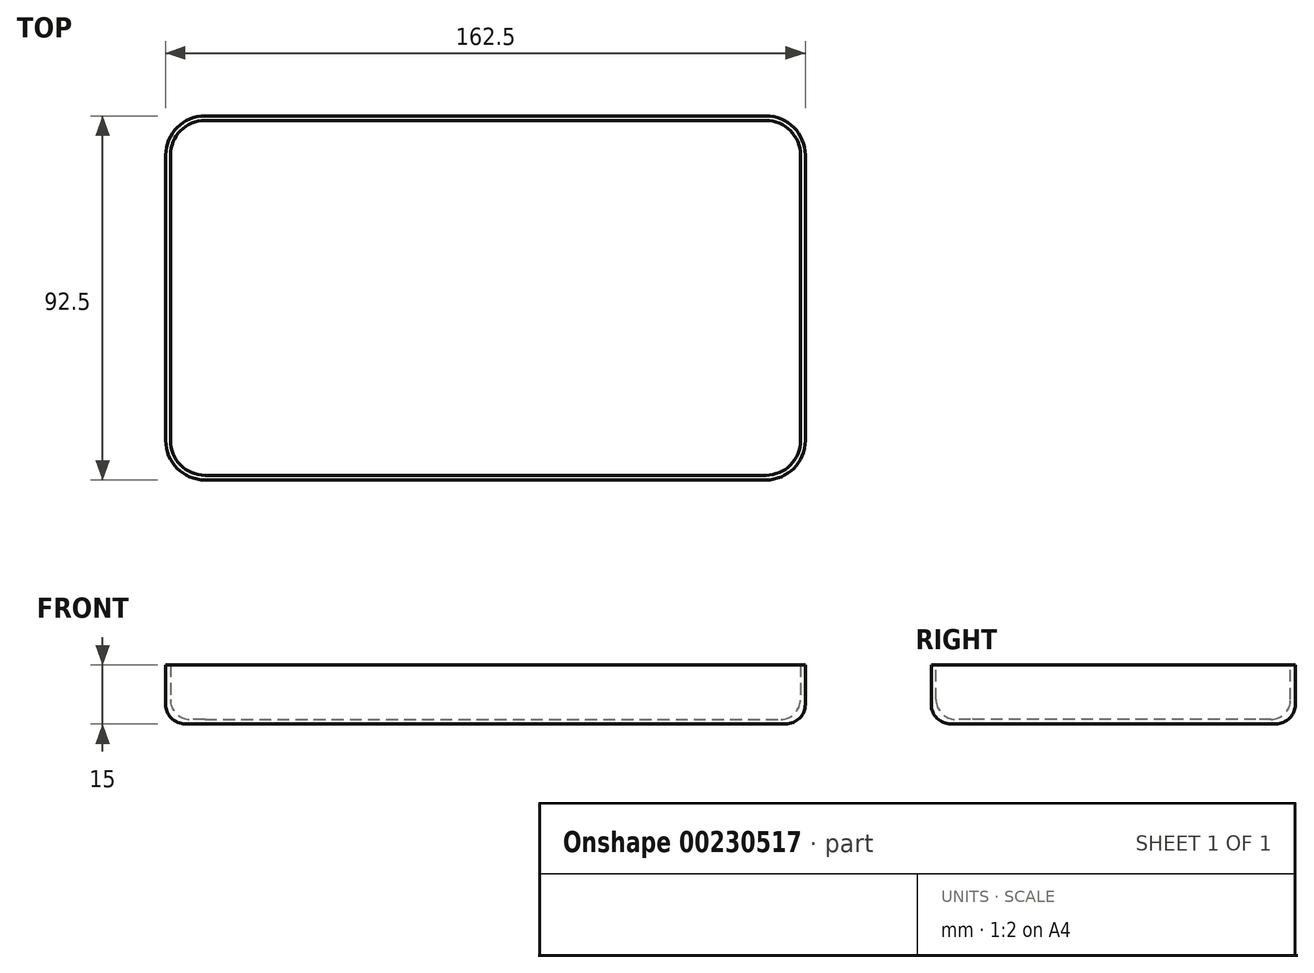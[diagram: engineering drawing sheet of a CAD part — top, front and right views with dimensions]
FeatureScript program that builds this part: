
annotation { "Feature Type Name" : "Feature", "Feature Type Description" : "" }
export const myFeature = defineFeature(function(context is Context, id is Id, definition is map)
    precondition{}
    {
        {
            var Q0;
            Q0=qCreatedBy(makeId("Top.planeOp"),FACE);
            var sketch = newSketch(context, id + "F0", { "sketchPlane" : qUnion([Q0])});
            skLineSegment(sketch, "E0.bottom", {"start": v(-107.19, 42.76) * mm, "end": v(35.31, 42.76) * mm});
            skLineSegment(sketch, "E0.top", {"start": v(-107.19, -49.74) * mm, "end": v(35.31, -49.74) * mm});
            skLineSegment(sketch, "E0.left", {"start": v(-117.19, 32.76) * mm, "end": v(-117.19, -39.74) * mm});
            skLineSegment(sketch, "E0.right", {"start": v(45.31, 32.76) * mm, "end": v(45.31, -39.74) * mm});
            skPoint(sketch, "E1.visualSharp", {"position": v(-117.19, 42.76) * mm});
            skArc(sketch, "E1.filletArc", {"start": v(-107.19, 42.76) * mm, "mid": v(-114.26, 39.84) * mm, "end": v(-117.19, 32.76) * mm});
            skPoint(sketch, "E2.visualSharp", {"position": v(-117.19, -49.74) * mm});
            skArc(sketch, "E2.filletArc", {"start": v(-117.19, -39.74) * mm, "mid": v(-114.26, -46.8) * mm, "end": v(-107.19, -49.74) * mm});
            skPoint(sketch, "E3.visualSharp", {"position": v(45.31, -49.74) * mm});
            skArc(sketch, "E3.filletArc", {"start": v(35.31, -49.74) * mm, "mid": v(42.38, -46.8) * mm, "end": v(45.31, -39.74) * mm});
            skPoint(sketch, "E4.visualSharp", {"position": v(45.31, 42.76) * mm});
            skArc(sketch, "E4.filletArc", {"start": v(45.31, 32.76) * mm, "mid": v(42.38, 39.84) * mm, "end": v(35.31, 42.76) * mm});
            skSolve(sketch);
        }
        {
            var Q0;
            Q0=qSketchRegion(id+"F0",true);
            extrude(context, id + "F1", {"entities" : qUnion([Q0]), "depth" : 15 * mm});
        }
        {
            var Q0;
            Q0=makeQuery(id+"F1.opExtrude","CAP_FACE",FACE,{"disambiguationData":[OSD([sQuery(id+"F0.wireOp",EDGE,"E0.bottom"),sQuery(id+"F0.wireOp",EDGE,"E0.top"),sQuery(id+"F0.wireOp",EDGE,"E0.left"),sQuery(id+"F0.wireOp",EDGE,"E0.right"),sQuery(id+"F0.wireOp",EDGE,"E1.filletArc"),sQuery(id+"F0.wireOp",EDGE,"E2.filletArc"),sQuery(id+"F0.wireOp",EDGE,"E3.filletArc"),sQuery(id+"F0.wireOp",EDGE,"E4.filletArc")])],"isStart":false});
            shell(context, id + "F2", {"entities" : qUnion([Q0]), "thickness" : 1.2 * mm});
        }
        {
            var Q0;
            Q0=makeQuery(id+"F2.opShell","OFFSET_FACE",FACE,{"disambiguationData":[OSD([sQuery(id+"F0.wireOp",EDGE,"E0.bottom"),sQuery(id+"F0.wireOp",EDGE,"E0.top"),sQuery(id+"F0.wireOp",EDGE,"E0.left"),sQuery(id+"F0.wireOp",EDGE,"E0.right"),sQuery(id+"F0.wireOp",EDGE,"E1.filletArc"),sQuery(id+"F0.wireOp",EDGE,"E2.filletArc"),sQuery(id+"F0.wireOp",EDGE,"E3.filletArc"),sQuery(id+"F0.wireOp",EDGE,"E4.filletArc")])]});
            fillet(context, id + "F3", {"entities" : qUnion([Q0]), "radius" : 5 * mm, "tangentPropagation" : true, "allowEdgeOverflow" : false});
        }
        {
            var Q0;
            Q0=makeQuery(id+"F1.opExtrude","CAP_FACE",FACE,{"disambiguationData":[OSD([sQuery(id+"F0.wireOp",EDGE,"E0.bottom"),sQuery(id+"F0.wireOp",EDGE,"E0.top"),sQuery(id+"F0.wireOp",EDGE,"E0.left"),sQuery(id+"F0.wireOp",EDGE,"E0.right"),sQuery(id+"F0.wireOp",EDGE,"E1.filletArc"),sQuery(id+"F0.wireOp",EDGE,"E2.filletArc"),sQuery(id+"F0.wireOp",EDGE,"E3.filletArc"),sQuery(id+"F0.wireOp",EDGE,"E4.filletArc")])],"isStart":true});
            fillet(context, id + "F4", {"entities" : qUnion([Q0]), "radius" : 5 * mm, "tangentPropagation" : true, "allowEdgeOverflow" : false});
        }
    });
